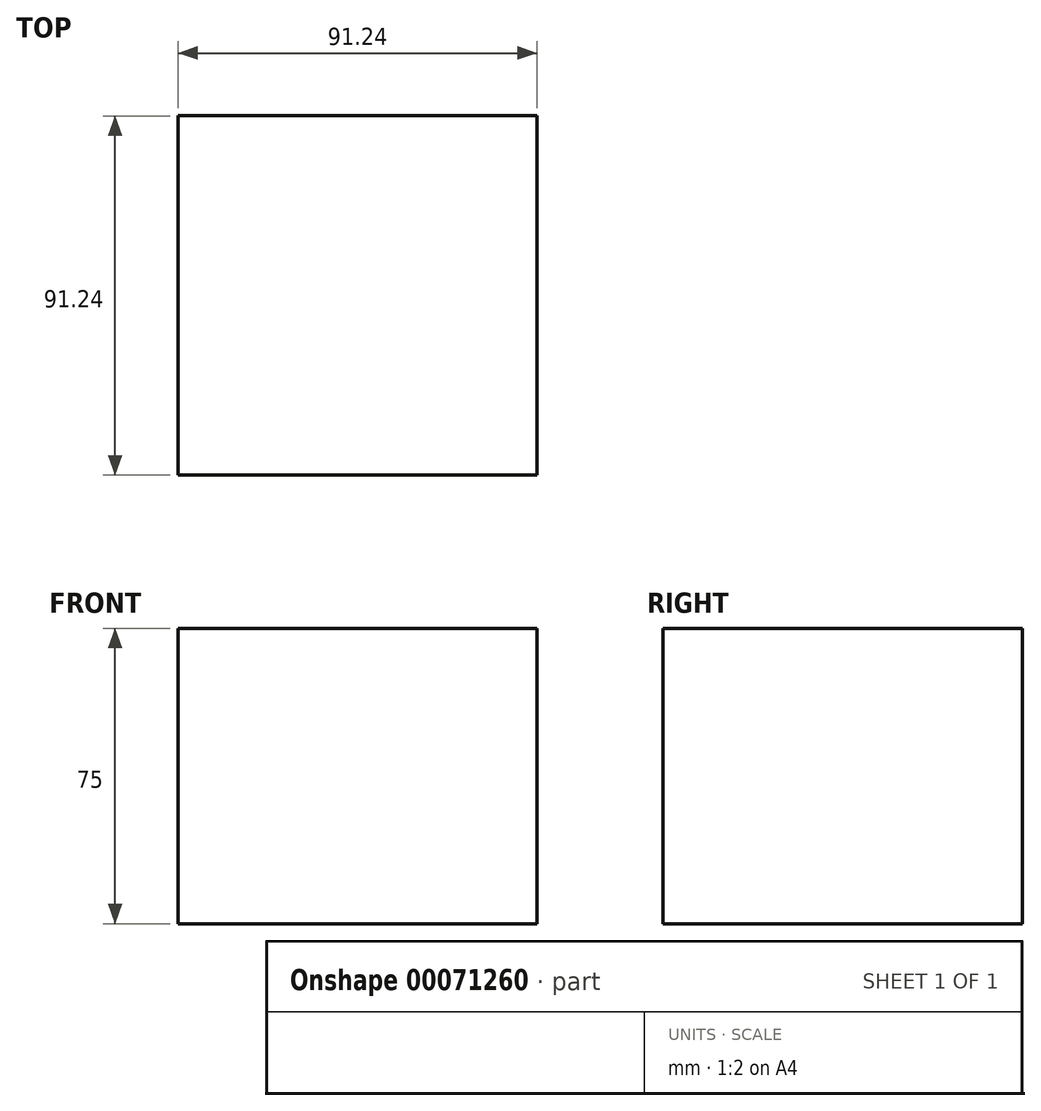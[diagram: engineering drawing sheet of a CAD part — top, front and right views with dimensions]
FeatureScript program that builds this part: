
annotation { "Feature Type Name" : "Feature", "Feature Type Description" : "" }
export const myFeature = defineFeature(function(context is Context, id is Id, definition is map)
    precondition{}
    {
        {
            var Q0;
            Q0=qCreatedBy(makeId("Top.planeOp"),FACE);
            var sketch = newSketch(context, id + "F0", { "sketchPlane" : qUnion([Q0])});
            skLineSegment(sketch, "E0.rect.bottom", {"start": v(-45.62, 45.62) * mm, "end": v(45.62, 45.62) * mm});
            skLineSegment(sketch, "E0.rect.top", {"start": v(-45.62, -45.62) * mm, "end": v(45.62, -45.62) * mm});
            skLineSegment(sketch, "E0.rect.left", {"start": v(-45.62, 45.62) * mm, "end": v(-45.62, -45.62) * mm});
            skLineSegment(sketch, "E0.rect.right", {"start": v(45.62, 45.62) * mm, "end": v(45.62, -45.62) * mm});
            skPoint(sketch, "E0.rect.middle", {"position": v(0, 0) * mm});
            skSolve(sketch);
        }
        {
            var Q0;
            Q0 = qSketchRegion(id + "F0", true);
            extrude(context, id + "F1", {"entities" : qUnion([Q0]), "endBound" : BoundingType.SYMMETRIC, "depth" : 75 * mm});
        }
    });
